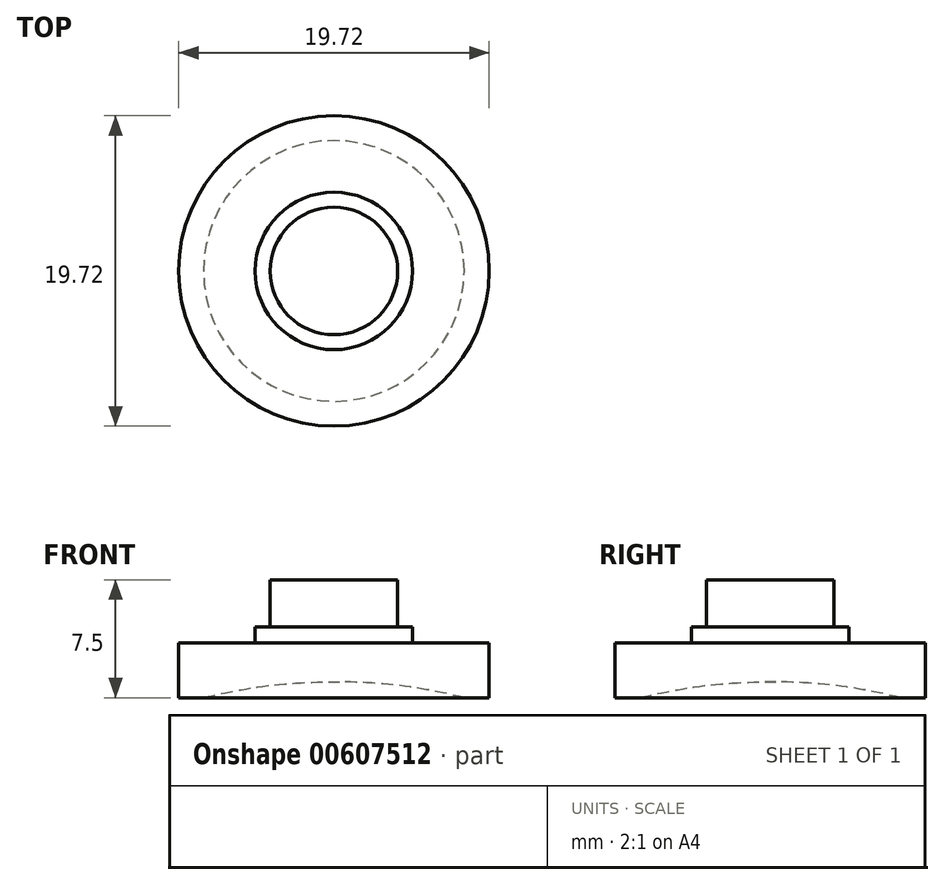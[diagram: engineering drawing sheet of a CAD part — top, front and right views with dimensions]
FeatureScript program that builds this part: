
annotation { "Feature Type Name" : "Feature", "Feature Type Description" : "" }
export const myFeature = defineFeature(function(context is Context, id is Id, definition is map)
    precondition{}
    {
        {
            var Q0;
            Q0=qCreatedBy(makeId("Top.planeOp"),FACE);
            var sketch = newSketch(context, id + "F0", { "sketchPlane" : qUnion([Q0])});
            skCircle(sketch, "E0", {"center": v(0, 0) * mm, "radius": 9.86 * mm});
            skSolve(sketch);
        }
        {
            var Q0;
            Q0=qSketchRegion(id+"F0",true);
            extrude(context, id + "F1", {"entities" : qUnion([Q0]), "depth" : 3.5 * mm, "offsetDistance" : 25 * mm});
        }
        {
            var Q0;
            Q0=makeQuery(id+"F1.opExtrude","CAP_FACE",FACE,{"disambiguationData":[OSD([sQuery(id+"F0.wireOp",EDGE,"E0")])],"isStart":false});
            var sketch = newSketch(context, id + "F2", { "sketchPlane" : qUnion([Q0])});
            skCircle(sketch, "E1", {"center": v(0, 0) * mm, "radius": 5 * mm});
            skSolve(sketch);
        }
        {
            var Q0;
            Q0=qSketchRegion(id+"F2",true);
            extrude(context, id + "F3", {"entities" : qUnion([Q0]), "operationType" : NewBodyOperationType.ADD, "depth" : 1 * mm, "offsetDistance" : 25 * mm});
        }
        {
            var Q0;
            Q0=makeQuery(id+"F3.opExtrude","CAP_FACE",FACE,{"disambiguationData":[OSD([sQuery(id+"F2.wireOp",EDGE,"E1")])],"isStart":false});
            var sketch = newSketch(context, id + "F4", { "sketchPlane" : qUnion([Q0])});
            skCircle(sketch, "E2", {"center": v(0, 0) * mm, "radius": 4.05 * mm});
            skSolve(sketch);
        }
        {
            var Q0;
            Q0=qSketchRegion(id+"F4",true);
            extrude(context, id + "F5", {"entities" : qUnion([Q0]), "operationType" : NewBodyOperationType.ADD, "depth" : 3 * mm, "offsetDistance" : 25 * mm});
        }
        {
            var Q0;
            Q0=makeQuery(id+"F1.opExtrude","CAP_FACE",FACE,{"disambiguationData":[OSD([sQuery(id+"F0.wireOp",EDGE,"E0")])],"isStart":true});
            var sketch = newSketch(context, id + "F6", { "sketchPlane" : qUnion([Q0])});
            skCircle(sketch, "E3", {"center": v(0, 0) * mm, "radius": 8.28 * mm});
            skSolve(sketch);
        }
        {
            var Q0;
            Q0=qSketchRegion(id+"F6",true);
            extrude(context, id + "F7", {"entities" : qUnion([Q0]), "operationType" : NewBodyOperationType.REMOVE, "oppositeDirection" : true, "depth" : 1 * mm, "offsetDistance" : 25 * mm});
        }
        {
            var Q0;
            Q0=makeQuery(id+"F7.boolean.opBoolean","COPY",EDGE,{"derivedFrom":makeQuery(id+"F7.opExtrude","CAP_EDGE",EDGE,{"disambiguationData":[OSD([sQuery(id+"F6.wireOp",EDGE,"E3")])],"isStart":false})});
            fillet(context, id + "F8", {"entities" : qUnion([Q0]), "radius" : 32 * mm, "tangentPropagation" : true, "allowEdgeOverflow" : false});
        }
    });
